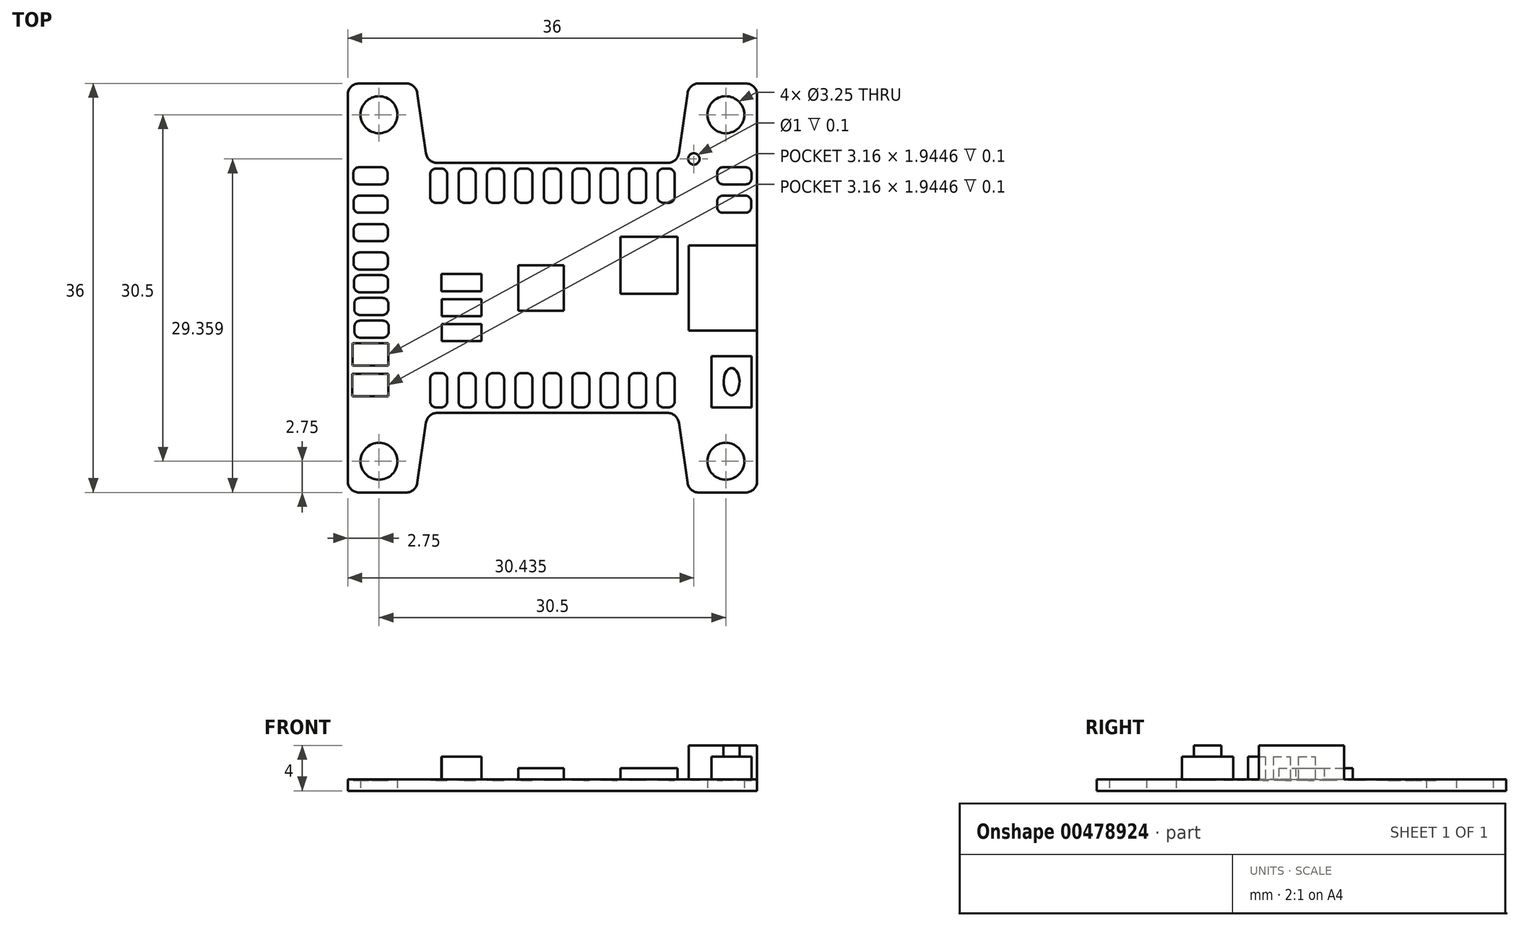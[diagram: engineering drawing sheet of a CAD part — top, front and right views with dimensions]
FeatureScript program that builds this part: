
annotation { "Feature Type Name" : "Feature", "Feature Type Description" : "" }
export const myFeature = defineFeature(function(context is Context, id is Id, definition is map)
    precondition{}
    {
        {
            var Q0;
            Q0=qCreatedBy(makeId("Top.planeOp"),FACE);
            var sketch = newSketch(context, id + "F0", { "sketchPlane" : qUnion([Q0])});
            skLineSegment(sketch, "E0.bottom", {"start": v(17, -18) * mm, "end": v(12.87, -18) * mm});
            skLineSegment(sketch, "E0.top", {"start": v(17, 18) * mm, "end": v(12.87, 18) * mm});
            skLineSegment(sketch, "E0.left", {"start": v(18, -17) * mm, "end": v(18, 17) * mm});
            skLineSegment(sketch, "E0.right", {"start": v(-18, -17) * mm, "end": v(-18, 17) * mm});
            skPoint(sketch, "E0.middle", {"position": v(0, 0) * mm});
            skLineSegment(sketch, "E1.bottom", {"start": v(15.25, 15.25) * mm, "end": v(-15.25, 15.25) * mm, "construction": true});
            skLineSegment(sketch, "E1.top", {"start": v(15.25, -15.25) * mm, "end": v(-15.25, -15.25) * mm, "construction": true});
            skLineSegment(sketch, "E1.left", {"start": v(15.25, 15.25) * mm, "end": v(15.25, -15.25) * mm, "construction": true});
            skLineSegment(sketch, "E1.right", {"start": v(-15.25, 15.25) * mm, "end": v(-15.25, -15.25) * mm, "construction": true});
            skCircle(sketch, "E2", {"center": v(-15.25, 15.25) * mm, "radius": 1.63 * mm});
            skCircle(sketch, "E3.MirrorC", {"center": v(15.25, 15.25) * mm, "radius": 1.63 * mm});
            skCircle(sketch, "E4.MirrorC", {"center": v(-15.25, -15.25) * mm, "radius": 1.63 * mm});
            skCircle(sketch, "E5.MirrorC", {"center": v(15.25, -15.25) * mm, "radius": 1.63 * mm});
            skLineSegment(sketch, "E6.left", {"start": v(18, -11) * mm, "end": v(18, 11) * mm});
            skLineSegment(sketch, "E6.right", {"start": v(-18, -11) * mm, "end": v(-18, 11) * mm});
            skLineSegment(sketch, "E7", {"start": v(-11.88, 17.14) * mm, "end": v(-11.12, 11.86) * mm});
            skLineSegment(sketch, "E8.MirrorCS", {"start": v(11.88, 17.14) * mm, "end": v(11.12, 11.86) * mm});
            skLineSegment(sketch, "E9.MirrorCS", {"start": v(-11.88, -17.14) * mm, "end": v(-11.12, -11.86) * mm});
            skLineSegment(sketch, "E10.MirrorCS", {"start": v(11.88, -17.14) * mm, "end": v(11.12, -11.86) * mm});
            skLineSegment(sketch, "E11.trimOffspring", {"start": v(10.13, 11) * mm, "end": v(-10.13, 11) * mm});
            skLineSegment(sketch, "E12.trimOffspring", {"start": v(10.13, -11) * mm, "end": v(-10.13, -11) * mm});
            skLineSegment(sketch, "E13.trimOffspring", {"start": v(-12.87, 18) * mm, "end": v(-17, 18) * mm});
            skLineSegment(sketch, "E14.trimOffspring", {"start": v(-12.87, -18) * mm, "end": v(-17, -18) * mm});
            skPoint(sketch, "E15.visualSharp", {"position": v(-18, 18) * mm});
            skArc(sketch, "E15.filletArc", {"start": v(-17, 18) * mm, "mid": v(-17.7, 17.7) * mm, "end": v(-18, 17) * mm});
            skPoint(sketch, "E16.visualSharp", {"position": v(-12, 18) * mm});
            skArc(sketch, "E16.filletArc", {"start": v(-11.88, 17.14) * mm, "mid": v(-12.21, 17.76) * mm, "end": v(-12.87, 18) * mm});
            skPoint(sketch, "E17.visualSharp", {"position": v(-11, 11) * mm});
            skArc(sketch, "E17.filletArc", {"start": v(-11.12, 11.86) * mm, "mid": v(-10.78, 11.24) * mm, "end": v(-10.13, 11) * mm});
            skPoint(sketch, "E18.visualSharp", {"position": v(12, 18) * mm});
            skArc(sketch, "E18.filletArc", {"start": v(12.87, 18) * mm, "mid": v(12.21, 17.76) * mm, "end": v(11.88, 17.14) * mm});
            skPoint(sketch, "E19.visualSharp", {"position": v(11, 11) * mm});
            skArc(sketch, "E19.filletArc", {"start": v(10.13, 11) * mm, "mid": v(10.78, 11.24) * mm, "end": v(11.12, 11.86) * mm});
            skPoint(sketch, "E20.visualSharp", {"position": v(18, 18) * mm});
            skArc(sketch, "E20.filletArc", {"start": v(18, 17) * mm, "mid": v(17.7, 17.7) * mm, "end": v(17, 18) * mm});
            skPoint(sketch, "E21.visualSharp", {"position": v(18, -18) * mm});
            skArc(sketch, "E21.filletArc", {"start": v(17, -18) * mm, "mid": v(17.7, -17.7) * mm, "end": v(18, -17) * mm});
            skPoint(sketch, "E22.visualSharp", {"position": v(12, -18) * mm});
            skArc(sketch, "E22.filletArc", {"start": v(11.88, -17.14) * mm, "mid": v(12.21, -17.76) * mm, "end": v(12.87, -18) * mm});
            skPoint(sketch, "E23.visualSharp", {"position": v(11, -11) * mm});
            skArc(sketch, "E23.filletArc", {"start": v(11.12, -11.86) * mm, "mid": v(10.78, -11.24) * mm, "end": v(10.13, -11) * mm});
            skPoint(sketch, "E24.visualSharp", {"position": v(-11, -11) * mm});
            skArc(sketch, "E24.filletArc", {"start": v(-10.13, -11) * mm, "mid": v(-10.78, -11.24) * mm, "end": v(-11.12, -11.86) * mm});
            skPoint(sketch, "E25.visualSharp", {"position": v(-12, -18) * mm});
            skArc(sketch, "E25.filletArc", {"start": v(-12.87, -18) * mm, "mid": v(-12.21, -17.76) * mm, "end": v(-11.88, -17.14) * mm});
            skPoint(sketch, "E26.visualSharp", {"position": v(-18, -18) * mm});
            skArc(sketch, "E26.filletArc", {"start": v(-18, -17) * mm, "mid": v(-17.7, -17.7) * mm, "end": v(-17, -18) * mm});
            skSolve(sketch);
        }
        {
            var Q0;
            Q0=makeQuery(id+"F0.imprint","IMPRINT",FACE,{"disambiguationData":[TD([[makeQuery(id+"F0.imprint","IMPRINT",EDGE,{"derivedFrom":sQuery(id+"F0.wireOp",EDGE,"E0.bottom")}),-1.0]])]});
            extrude(context, id + "F1", {"entities" : qUnion([Q0]), "depth" : 1 * mm, "offsetDistance" : 25 * mm});
        }
        {
            var Q0;
            Q0=makeQuery(id+"F1.opExtrude","CAP_FACE",FACE,{"disambiguationData":[OSD([sQuery(id+"F0.wireOp",EDGE,"E0.bottom"),sQuery(id+"F0.wireOp",EDGE,"E0.top"),sQuery(id+"F0.wireOp",EDGE,"E0.left"),sQuery(id+"F0.wireOp",EDGE,"E0.right"),sQuery(id+"F0.wireOp",EDGE,"E2"),sQuery(id+"F0.wireOp",EDGE,"E3.MirrorC"),sQuery(id+"F0.wireOp",EDGE,"E4.MirrorC"),sQuery(id+"F0.wireOp",EDGE,"E5.MirrorC"),sQuery(id+"F0.wireOp",EDGE,"E7"),sQuery(id+"F0.wireOp",EDGE,"E8.MirrorCS"),sQuery(id+"F0.wireOp",EDGE,"E9.MirrorCS"),sQuery(id+"F0.wireOp",EDGE,"E10.MirrorCS"),sQuery(id+"F0.wireOp",EDGE,"E11.trimOffspring"),sQuery(id+"F0.wireOp",EDGE,"E12.trimOffspring"),sQuery(id+"F0.wireOp",EDGE,"E13.trimOffspring"),sQuery(id+"F0.wireOp",EDGE,"E14.trimOffspring"),sQuery(id+"F0.wireOp",EDGE,"E15.filletArc"),sQuery(id+"F0.wireOp",EDGE,"E16.filletArc"),sQuery(id+"F0.wireOp",EDGE,"E17.filletArc"),sQuery(id+"F0.wireOp",EDGE,"E18.filletArc"),sQuery(id+"F0.wireOp",EDGE,"E19.filletArc"),sQuery(id+"F0.wireOp",EDGE,"E20.filletArc"),sQuery(id+"F0.wireOp",EDGE,"E21.filletArc"),sQuery(id+"F0.wireOp",EDGE,"E22.filletArc"),sQuery(id+"F0.wireOp",EDGE,"E23.filletArc"),sQuery(id+"F0.wireOp",EDGE,"E24.filletArc"),sQuery(id+"F0.wireOp",EDGE,"E25.filletArc"),sQuery(id+"F0.wireOp",EDGE,"E26.filletArc")])],"isStart":false});
            var sketch = newSketch(context, id + "F2", { "sketchPlane" : qUnion([Q0])});
            skLineSegment(sketch, "E27.bottom", {"start": v(0.25, 7.5) * mm, "end": v(-0.25, 7.5) * mm});
            skLineSegment(sketch, "E27.top", {"start": v(0.25, 10.5) * mm, "end": v(-0.25, 10.5) * mm});
            skLineSegment(sketch, "E27.left", {"start": v(0.75, 8) * mm, "end": v(0.75, 10) * mm});
            skLineSegment(sketch, "E27.right", {"start": v(-0.75, 8) * mm, "end": v(-0.75, 10) * mm});
            skPoint(sketch, "E27.middle", {"position": v(0, 9) * mm});
            skPoint(sketch, "E28.visualSharp", {"position": v(-0.75, 10.5) * mm});
            skArc(sketch, "E28.filletArc", {"start": v(-0.25, 10.5) * mm, "mid": v(-0.6, 10.35) * mm, "end": v(-0.75, 10) * mm});
            skPoint(sketch, "E29.visualSharp", {"position": v(0.75, 10.5) * mm});
            skArc(sketch, "E29.filletArc", {"start": v(0.75, 10) * mm, "mid": v(0.6, 10.35) * mm, "end": v(0.25, 10.5) * mm});
            skPoint(sketch, "E30.visualSharp", {"position": v(0.75, 7.5) * mm});
            skArc(sketch, "E30.filletArc", {"start": v(0.25, 7.5) * mm, "mid": v(0.6, 7.65) * mm, "end": v(0.75, 8) * mm});
            skPoint(sketch, "E31.visualSharp", {"position": v(-0.75, 7.5) * mm});
            skArc(sketch, "E31.filletArc", {"start": v(-0.75, 8) * mm, "mid": v(-0.6, 7.65) * mm, "end": v(-0.25, 7.5) * mm});
            skLineSegment(sketch, "E32.1.0.0", {"start": v(3.25, 8) * mm, "end": v(3.25, 10) * mm});
            skPoint(sketch, "E32.1.0.1", {"position": v(3.25, 7.5) * mm});
            skLineSegment(sketch, "E32.1.0.2", {"start": v(1.75, 8) * mm, "end": v(1.75, 10) * mm});
            skArc(sketch, "E32.1.0.3", {"start": v(2.75, 7.5) * mm, "mid": v(3.1, 7.65) * mm, "end": v(3.25, 8) * mm});
            skPoint(sketch, "E32.1.0.4", {"position": v(1.75, 10.5) * mm});
            skArc(sketch, "E32.1.0.5", {"start": v(2.25, 10.5) * mm, "mid": v(1.9, 10.35) * mm, "end": v(1.75, 10) * mm});
            skPoint(sketch, "E32.1.0.6", {"position": v(3.25, 10.5) * mm});
            skArc(sketch, "E32.1.0.7", {"start": v(1.75, 8) * mm, "mid": v(1.9, 7.65) * mm, "end": v(2.25, 7.5) * mm});
            skLineSegment(sketch, "E32.1.0.8", {"start": v(2.75, 10.5) * mm, "end": v(2.25, 10.5) * mm});
            skLineSegment(sketch, "E32.1.0.9", {"start": v(2.75, 7.5) * mm, "end": v(2.25, 7.5) * mm});
            skPoint(sketch, "E32.1.0.10", {"position": v(2.5, 9) * mm});
            skPoint(sketch, "E32.1.0.11", {"position": v(1.75, 7.5) * mm});
            skArc(sketch, "E32.1.0.12", {"start": v(3.25, 10) * mm, "mid": v(3.1, 10.35) * mm, "end": v(2.75, 10.5) * mm});
            skLineSegment(sketch, "E32.2.0.0", {"start": v(5.75, 8) * mm, "end": v(5.75, 10) * mm});
            skPoint(sketch, "E32.2.0.1", {"position": v(5.75, 7.5) * mm});
            skLineSegment(sketch, "E32.2.0.2", {"start": v(4.25, 8) * mm, "end": v(4.25, 10) * mm});
            skArc(sketch, "E32.2.0.3", {"start": v(5.25, 7.5) * mm, "mid": v(5.6, 7.65) * mm, "end": v(5.75, 8) * mm});
            skPoint(sketch, "E32.2.0.4", {"position": v(4.25, 10.5) * mm});
            skArc(sketch, "E32.2.0.5", {"start": v(4.75, 10.5) * mm, "mid": v(4.4, 10.35) * mm, "end": v(4.25, 10) * mm});
            skPoint(sketch, "E32.2.0.6", {"position": v(5.75, 10.5) * mm});
            skArc(sketch, "E32.2.0.7", {"start": v(4.25, 8) * mm, "mid": v(4.4, 7.65) * mm, "end": v(4.75, 7.5) * mm});
            skLineSegment(sketch, "E32.2.0.8", {"start": v(5.25, 10.5) * mm, "end": v(4.75, 10.5) * mm});
            skLineSegment(sketch, "E32.2.0.9", {"start": v(5.25, 7.5) * mm, "end": v(4.75, 7.5) * mm});
            skPoint(sketch, "E32.2.0.10", {"position": v(5, 9) * mm});
            skPoint(sketch, "E32.2.0.11", {"position": v(4.25, 7.5) * mm});
            skArc(sketch, "E32.2.0.12", {"start": v(5.75, 10) * mm, "mid": v(5.6, 10.35) * mm, "end": v(5.25, 10.5) * mm});
            skLineSegment(sketch, "E32.3.0.0", {"start": v(8.25, 8) * mm, "end": v(8.25, 10) * mm});
            skPoint(sketch, "E32.3.0.1", {"position": v(8.25, 7.5) * mm});
            skLineSegment(sketch, "E32.3.0.2", {"start": v(6.75, 8) * mm, "end": v(6.75, 10) * mm});
            skArc(sketch, "E32.3.0.3", {"start": v(7.75, 7.5) * mm, "mid": v(8.1, 7.65) * mm, "end": v(8.25, 8) * mm});
            skPoint(sketch, "E32.3.0.4", {"position": v(6.75, 10.5) * mm});
            skArc(sketch, "E32.3.0.5", {"start": v(7.25, 10.5) * mm, "mid": v(6.9, 10.35) * mm, "end": v(6.75, 10) * mm});
            skPoint(sketch, "E32.3.0.6", {"position": v(8.25, 10.5) * mm});
            skArc(sketch, "E32.3.0.7", {"start": v(6.75, 8) * mm, "mid": v(6.9, 7.65) * mm, "end": v(7.25, 7.5) * mm});
            skLineSegment(sketch, "E32.3.0.8", {"start": v(7.75, 10.5) * mm, "end": v(7.25, 10.5) * mm});
            skLineSegment(sketch, "E32.3.0.9", {"start": v(7.75, 7.5) * mm, "end": v(7.25, 7.5) * mm});
            skPoint(sketch, "E32.3.0.10", {"position": v(7.5, 9) * mm});
            skPoint(sketch, "E32.3.0.11", {"position": v(6.75, 7.5) * mm});
            skArc(sketch, "E32.3.0.12", {"start": v(8.25, 10) * mm, "mid": v(8.1, 10.35) * mm, "end": v(7.75, 10.5) * mm});
            skLineSegment(sketch, "E32.4.0.0", {"start": v(10.75, 8) * mm, "end": v(10.75, 10) * mm});
            skPoint(sketch, "E32.4.0.1", {"position": v(10.75, 7.5) * mm});
            skLineSegment(sketch, "E32.4.0.2", {"start": v(9.25, 8) * mm, "end": v(9.25, 10) * mm});
            skArc(sketch, "E32.4.0.3", {"start": v(10.25, 7.5) * mm, "mid": v(10.6, 7.65) * mm, "end": v(10.75, 8) * mm});
            skPoint(sketch, "E32.4.0.4", {"position": v(9.25, 10.5) * mm});
            skArc(sketch, "E32.4.0.5", {"start": v(9.75, 10.5) * mm, "mid": v(9.4, 10.35) * mm, "end": v(9.25, 10) * mm});
            skPoint(sketch, "E32.4.0.6", {"position": v(10.75, 10.5) * mm});
            skArc(sketch, "E32.4.0.7", {"start": v(9.25, 8) * mm, "mid": v(9.4, 7.65) * mm, "end": v(9.75, 7.5) * mm});
            skLineSegment(sketch, "E32.4.0.8", {"start": v(10.25, 10.5) * mm, "end": v(9.75, 10.5) * mm});
            skLineSegment(sketch, "E32.4.0.9", {"start": v(10.25, 7.5) * mm, "end": v(9.75, 7.5) * mm});
            skPoint(sketch, "E32.4.0.10", {"position": v(10, 9) * mm});
            skPoint(sketch, "E32.4.0.11", {"position": v(9.25, 7.5) * mm});
            skArc(sketch, "E32.4.0.12", {"start": v(10.75, 10) * mm, "mid": v(10.6, 10.35) * mm, "end": v(10.25, 10.5) * mm});
            skLineSegment(sketch, "E32.direction1", {"start": v(-0.75, 7.5) * mm, "end": v(1.75, 7.5) * mm, "construction": true});
            skArc(sketch, "E33.MirrorCS", {"start": v(-9.25, 8) * mm, "mid": v(-9.4, 7.65) * mm, "end": v(-9.75, 7.5) * mm});
            skLineSegment(sketch, "E34.MirrorCS", {"start": v(-7.75, 10.5) * mm, "end": v(-7.25, 10.5) * mm});
            skArc(sketch, "E35.MirrorCS", {"start": v(-4.25, 8) * mm, "mid": v(-4.4, 7.65) * mm, "end": v(-4.75, 7.5) * mm});
            skArc(sketch, "E36.MirrorCS", {"start": v(-7.25, 10.5) * mm, "mid": v(-6.9, 10.35) * mm, "end": v(-6.75, 10) * mm});
            skArc(sketch, "E37.MirrorCS", {"start": v(-9.75, 10.5) * mm, "mid": v(-9.4, 10.35) * mm, "end": v(-9.25, 10) * mm});
            skArc(sketch, "E38.MirrorCS", {"start": v(-4.75, 10.5) * mm, "mid": v(-4.4, 10.35) * mm, "end": v(-4.25, 10) * mm});
            skArc(sketch, "E39.MirrorCS", {"start": v(-7.75, 7.5) * mm, "mid": v(-8.1, 7.65) * mm, "end": v(-8.25, 8) * mm});
            skArc(sketch, "E40.MirrorCS", {"start": v(-1.75, 8) * mm, "mid": v(-1.9, 7.65) * mm, "end": v(-2.25, 7.5) * mm});
            skArc(sketch, "E41.MirrorCS", {"start": v(-2.25, 10.5) * mm, "mid": v(-1.9, 10.35) * mm, "end": v(-1.75, 10) * mm});
            skArc(sketch, "E42.MirrorCS", {"start": v(-2.75, 7.5) * mm, "mid": v(-3.1, 7.65) * mm, "end": v(-3.25, 8) * mm});
            skArc(sketch, "E43.MirrorCS", {"start": v(-10.25, 7.5) * mm, "mid": v(-10.6, 7.65) * mm, "end": v(-10.75, 8) * mm});
            skArc(sketch, "E44.MirrorCS", {"start": v(-3.25, 10) * mm, "mid": v(-3.1, 10.35) * mm, "end": v(-2.75, 10.5) * mm});
            skLineSegment(sketch, "E45.MirrorCS", {"start": v(-2.75, 7.5) * mm, "end": v(-2.25, 7.5) * mm});
            skArc(sketch, "E46.MirrorCS", {"start": v(-5.25, 7.5) * mm, "mid": v(-5.6, 7.65) * mm, "end": v(-5.75, 8) * mm});
            skLineSegment(sketch, "E47.MirrorCS", {"start": v(-2.75, 10.5) * mm, "end": v(-2.25, 10.5) * mm});
            skArc(sketch, "E48.MirrorCS", {"start": v(-5.75, 10) * mm, "mid": v(-5.6, 10.35) * mm, "end": v(-5.25, 10.5) * mm});
            skArc(sketch, "E49.MirrorCS", {"start": v(-10.75, 10) * mm, "mid": v(-10.6, 10.35) * mm, "end": v(-10.25, 10.5) * mm});
            skLineSegment(sketch, "E50.MirrorCS", {"start": v(-10.25, 7.5) * mm, "end": v(-9.75, 7.5) * mm});
            skArc(sketch, "E51.MirrorCS", {"start": v(-8.25, 10) * mm, "mid": v(-8.1, 10.35) * mm, "end": v(-7.75, 10.5) * mm});
            skLineSegment(sketch, "E52.MirrorCS", {"start": v(-5.25, 10.5) * mm, "end": v(-4.75, 10.5) * mm});
            skArc(sketch, "E53.MirrorCS", {"start": v(-6.75, 8) * mm, "mid": v(-6.9, 7.65) * mm, "end": v(-7.25, 7.5) * mm});
            skLineSegment(sketch, "E54.MirrorCS", {"start": v(-7.75, 7.5) * mm, "end": v(-7.25, 7.5) * mm});
            skLineSegment(sketch, "E55.MirrorCS", {"start": v(-5.25, 7.5) * mm, "end": v(-4.75, 7.5) * mm});
            skLineSegment(sketch, "E56.MirrorCS", {"start": v(-10.25, 10.5) * mm, "end": v(-9.75, 10.5) * mm});
            skLineSegment(sketch, "E57.MirrorCS", {"start": v(0.75, 7.5) * mm, "end": v(-1.75, 7.5) * mm, "construction": true});
            skPoint(sketch, "E58.MirrorP", {"position": v(-3.25, 7.5) * mm});
            skPoint(sketch, "E59.MirrorP", {"position": v(-4.25, 7.5) * mm});
            skPoint(sketch, "E60.MirrorP", {"position": v(-5.75, 7.5) * mm});
            skPoint(sketch, "E61.MirrorP", {"position": v(-1.75, 10.5) * mm});
            skPoint(sketch, "E62.MirrorP", {"position": v(-6.75, 7.5) * mm});
            skPoint(sketch, "E63.MirrorP", {"position": v(-8.25, 7.5) * mm});
            skPoint(sketch, "E64.MirrorP", {"position": v(-9.25, 7.5) * mm});
            skPoint(sketch, "E65.MirrorP", {"position": v(-10.75, 10.5) * mm});
            skPoint(sketch, "E66.MirrorP", {"position": v(-5, 9) * mm});
            skLineSegment(sketch, "E67.MirrorCS", {"start": v(-1.75, 8) * mm, "end": v(-1.75, 10) * mm});
            skLineSegment(sketch, "E68.MirrorCS", {"start": v(-3.25, 8) * mm, "end": v(-3.25, 10) * mm});
            skPoint(sketch, "E69.MirrorP", {"position": v(-7.5, 9) * mm});
            skLineSegment(sketch, "E70.MirrorCS", {"start": v(-6.75, 8) * mm, "end": v(-6.75, 10) * mm});
            skPoint(sketch, "E71.MirrorP", {"position": v(-1.75, 7.5) * mm});
            skLineSegment(sketch, "E72.MirrorCS", {"start": v(-9.25, 8) * mm, "end": v(-9.25, 10) * mm});
            skPoint(sketch, "E73.MirrorP", {"position": v(-5.75, 10.5) * mm});
            skLineSegment(sketch, "E74.MirrorCS", {"start": v(-4.25, 8) * mm, "end": v(-4.25, 10) * mm});
            skPoint(sketch, "E75.MirrorP", {"position": v(-2.5, 9) * mm});
            skPoint(sketch, "E76.MirrorP", {"position": v(-8.25, 10.5) * mm});
            skLineSegment(sketch, "E77.MirrorCS", {"start": v(-8.25, 8) * mm, "end": v(-8.25, 10) * mm});
            skPoint(sketch, "E78.MirrorP", {"position": v(-9.25, 10.5) * mm});
            skLineSegment(sketch, "E79.MirrorCS", {"start": v(-5.75, 8) * mm, "end": v(-5.75, 10) * mm});
            skLineSegment(sketch, "E80.MirrorCS", {"start": v(-10.75, 8) * mm, "end": v(-10.75, 10) * mm});
            skPoint(sketch, "E81.MirrorP", {"position": v(-10, 9) * mm});
            skPoint(sketch, "E82.MirrorP", {"position": v(-6.75, 10.5) * mm});
            skPoint(sketch, "E83.MirrorP", {"position": v(-4.25, 10.5) * mm});
            skPoint(sketch, "E84.MirrorP", {"position": v(-3.25, 10.5) * mm});
            skPoint(sketch, "E85.MirrorP", {"position": v(-10.75, 7.5) * mm});
            skArc(sketch, "E86.MirrorCS", {"start": v(9.25, -8) * mm, "mid": v(9.4, -7.65) * mm, "end": v(9.75, -7.5) * mm});
            skLineSegment(sketch, "E87.MirrorCS", {"start": v(7.75, -10.5) * mm, "end": v(7.25, -10.5) * mm});
            skArc(sketch, "E88.MirrorCS", {"start": v(-3.25, -10) * mm, "mid": v(-3.1, -10.35) * mm, "end": v(-2.75, -10.5) * mm});
            skArc(sketch, "E89.MirrorCS", {"start": v(-9.75, -10.5) * mm, "mid": v(-9.4, -10.35) * mm, "end": v(-9.25, -10) * mm});
            skArc(sketch, "E90.MirrorCS", {"start": v(4.25, -8) * mm, "mid": v(4.4, -7.65) * mm, "end": v(4.75, -7.5) * mm});
            skArc(sketch, "E91.MirrorCS", {"start": v(7.25, -10.5) * mm, "mid": v(6.9, -10.35) * mm, "end": v(6.75, -10) * mm});
            skArc(sketch, "E92.MirrorCS", {"start": v(-4.25, -8) * mm, "mid": v(-4.4, -7.65) * mm, "end": v(-4.75, -7.5) * mm});
            skArc(sketch, "E93.MirrorCS", {"start": v(-8.25, -10) * mm, "mid": v(-8.1, -10.35) * mm, "end": v(-7.75, -10.5) * mm});
            skArc(sketch, "E94.MirrorCS", {"start": v(9.75, -10.5) * mm, "mid": v(9.4, -10.35) * mm, "end": v(9.25, -10) * mm});
            skArc(sketch, "E95.MirrorCS", {"start": v(-10.25, -7.5) * mm, "mid": v(-10.6, -7.65) * mm, "end": v(-10.75, -8) * mm});
            skArc(sketch, "E96.MirrorCS", {"start": v(4.75, -10.5) * mm, "mid": v(4.4, -10.35) * mm, "end": v(4.25, -10) * mm});
            skArc(sketch, "E97.MirrorCS", {"start": v(7.75, -7.5) * mm, "mid": v(8.1, -7.65) * mm, "end": v(8.25, -8) * mm});
            skLineSegment(sketch, "E98.MirrorCS", {"start": v(-7.75, -10.5) * mm, "end": v(-7.25, -10.5) * mm});
            skLineSegment(sketch, "E99.MirrorCS", {"start": v(-10.25, -7.5) * mm, "end": v(-9.75, -7.5) * mm});
            skArc(sketch, "E100.MirrorCS", {"start": v(1.75, -8) * mm, "mid": v(1.9, -7.65) * mm, "end": v(2.25, -7.5) * mm});
            skArc(sketch, "E101.MirrorCS", {"start": v(2.25, -10.5) * mm, "mid": v(1.9, -10.35) * mm, "end": v(1.75, -10) * mm});
            skArc(sketch, "E102.MirrorCS", {"start": v(2.75, -7.5) * mm, "mid": v(3.1, -7.65) * mm, "end": v(3.25, -8) * mm});
            skArc(sketch, "E103.MirrorCS", {"start": v(-0.75, -8) * mm, "mid": v(-0.6, -7.65) * mm, "end": v(-0.25, -7.5) * mm});
            skArc(sketch, "E104.MirrorCS", {"start": v(0.25, -7.5) * mm, "mid": v(0.6, -7.65) * mm, "end": v(0.75, -8) * mm});
            skArc(sketch, "E105.MirrorCS", {"start": v(0.75, -10) * mm, "mid": v(0.6, -10.35) * mm, "end": v(0.25, -10.5) * mm});
            skArc(sketch, "E106.MirrorCS", {"start": v(-0.25, -10.5) * mm, "mid": v(-0.6, -10.35) * mm, "end": v(-0.75, -10) * mm});
            skLineSegment(sketch, "E107.MirrorCS", {"start": v(0.25, -10.5) * mm, "end": v(-0.25, -10.5) * mm});
            skLineSegment(sketch, "E108.MirrorCS", {"start": v(0.25, -7.5) * mm, "end": v(-0.25, -7.5) * mm});
            skArc(sketch, "E109.MirrorCS", {"start": v(10.25, -7.5) * mm, "mid": v(10.6, -7.65) * mm, "end": v(10.75, -8) * mm});
            skArc(sketch, "E110.MirrorCS", {"start": v(-2.75, -7.5) * mm, "mid": v(-3.1, -7.65) * mm, "end": v(-3.25, -8) * mm});
            skArc(sketch, "E111.MirrorCS", {"start": v(3.25, -10) * mm, "mid": v(3.1, -10.35) * mm, "end": v(2.75, -10.5) * mm});
            skArc(sketch, "E112.MirrorCS", {"start": v(5.25, -7.5) * mm, "mid": v(5.6, -7.65) * mm, "end": v(5.75, -8) * mm});
            skLineSegment(sketch, "E113.MirrorCS", {"start": v(-5.25, -10.5) * mm, "end": v(-4.75, -10.5) * mm});
            skArc(sketch, "E114.MirrorCS", {"start": v(-7.25, -10.5) * mm, "mid": v(-6.9, -10.35) * mm, "end": v(-6.75, -10) * mm});
            skArc(sketch, "E115.MirrorCS", {"start": v(6.75, -8) * mm, "mid": v(6.9, -7.65) * mm, "end": v(7.25, -7.5) * mm});
            skLineSegment(sketch, "E116.MirrorCS", {"start": v(5.25, -10.5) * mm, "end": v(4.75, -10.5) * mm});
            skLineSegment(sketch, "E117.MirrorCS", {"start": v(-7.75, -7.5) * mm, "end": v(-7.25, -7.5) * mm});
            skLineSegment(sketch, "E118.MirrorCS", {"start": v(-2.75, -7.5) * mm, "end": v(-2.25, -7.5) * mm});
            skArc(sketch, "E119.MirrorCS", {"start": v(-4.75, -10.5) * mm, "mid": v(-4.4, -10.35) * mm, "end": v(-4.25, -10) * mm});
            skLineSegment(sketch, "E120.MirrorCS", {"start": v(10.25, -10.5) * mm, "end": v(9.75, -10.5) * mm});
            skLineSegment(sketch, "E121.MirrorCS", {"start": v(7.75, -7.5) * mm, "end": v(7.25, -7.5) * mm});
            skLineSegment(sketch, "E122.MirrorCS", {"start": v(5.25, -7.5) * mm, "end": v(4.75, -7.5) * mm});
            skLineSegment(sketch, "E123.MirrorCS", {"start": v(-5.25, -7.5) * mm, "end": v(-4.75, -7.5) * mm});
            skArc(sketch, "E124.MirrorCS", {"start": v(-7.75, -7.5) * mm, "mid": v(-8.1, -7.65) * mm, "end": v(-8.25, -8) * mm});
            skArc(sketch, "E125.MirrorCS", {"start": v(-5.25, -7.5) * mm, "mid": v(-5.6, -7.65) * mm, "end": v(-5.75, -8) * mm});
            skLineSegment(sketch, "E126.MirrorCS", {"start": v(10.25, -7.5) * mm, "end": v(9.75, -7.5) * mm});
            skArc(sketch, "E127.MirrorCS", {"start": v(8.25, -10) * mm, "mid": v(8.1, -10.35) * mm, "end": v(7.75, -10.5) * mm});
            skLineSegment(sketch, "E128.MirrorCS", {"start": v(-10.25, -10.5) * mm, "end": v(-9.75, -10.5) * mm});
            skArc(sketch, "E129.MirrorCS", {"start": v(-1.75, -8) * mm, "mid": v(-1.9, -7.65) * mm, "end": v(-2.25, -7.5) * mm});
            skLineSegment(sketch, "E130.MirrorCS", {"start": v(-2.75, -10.5) * mm, "end": v(-2.25, -10.5) * mm});
            skArc(sketch, "E131.MirrorCS", {"start": v(10.75, -10) * mm, "mid": v(10.6, -10.35) * mm, "end": v(10.25, -10.5) * mm});
            skArc(sketch, "E132.MirrorCS", {"start": v(5.75, -10) * mm, "mid": v(5.6, -10.35) * mm, "end": v(5.25, -10.5) * mm});
            skArc(sketch, "E133.MirrorCS", {"start": v(-5.75, -10) * mm, "mid": v(-5.6, -10.35) * mm, "end": v(-5.25, -10.5) * mm});
            skLineSegment(sketch, "E134.MirrorCS", {"start": v(2.75, -10.5) * mm, "end": v(2.25, -10.5) * mm});
            skLineSegment(sketch, "E135.MirrorCS", {"start": v(2.75, -7.5) * mm, "end": v(2.25, -7.5) * mm});
            skArc(sketch, "E136.MirrorCS", {"start": v(-2.25, -10.5) * mm, "mid": v(-1.9, -10.35) * mm, "end": v(-1.75, -10) * mm});
            skArc(sketch, "E137.MirrorCS", {"start": v(-9.25, -8) * mm, "mid": v(-9.4, -7.65) * mm, "end": v(-9.75, -7.5) * mm});
            skArc(sketch, "E138.MirrorCS", {"start": v(-10.75, -10) * mm, "mid": v(-10.6, -10.35) * mm, "end": v(-10.25, -10.5) * mm});
            skArc(sketch, "E139.MirrorCS", {"start": v(-6.75, -8) * mm, "mid": v(-6.9, -7.65) * mm, "end": v(-7.25, -7.5) * mm});
            skLineSegment(sketch, "E140.MirrorCS", {"start": v(-0.75, -7.5) * mm, "end": v(1.75, -7.5) * mm, "construction": true});
            skLineSegment(sketch, "E141.MirrorCS", {"start": v(0.75, -7.5) * mm, "end": v(-1.75, -7.5) * mm, "construction": true});
            skPoint(sketch, "E142.MirrorP", {"position": v(-1.75, -7.5) * mm});
            skPoint(sketch, "E143.MirrorP", {"position": v(-0.75, -7.5) * mm});
            skLineSegment(sketch, "E144.MirrorCS", {"start": v(-6.75, -8) * mm, "end": v(-6.75, -10) * mm});
            skPoint(sketch, "E145.MirrorP", {"position": v(-1.75, -10.5) * mm});
            skPoint(sketch, "E146.MirrorP", {"position": v(-2.5, -9) * mm});
            skPoint(sketch, "E147.MirrorP", {"position": v(-10.75, -7.5) * mm});
            skPoint(sketch, "E148.MirrorP", {"position": v(0, -9) * mm});
            skPoint(sketch, "E149.MirrorP", {"position": v(1.75, -7.5) * mm});
            skPoint(sketch, "E150.MirrorP", {"position": v(3.25, -7.5) * mm});
            skPoint(sketch, "E151.MirrorP", {"position": v(4.25, -7.5) * mm});
            skPoint(sketch, "E152.MirrorP", {"position": v(9.25, -10.5) * mm});
            skPoint(sketch, "E153.MirrorP", {"position": v(-7.5, -9) * mm});
            skPoint(sketch, "E154.MirrorP", {"position": v(5.75, -10.5) * mm});
            skLineSegment(sketch, "E155.MirrorCS", {"start": v(-3.25, -8) * mm, "end": v(-3.25, -10) * mm});
            skPoint(sketch, "E156.MirrorP", {"position": v(-5.75, -7.5) * mm});
            skPoint(sketch, "E157.MirrorP", {"position": v(-3.25, -10.5) * mm});
            skLineSegment(sketch, "E158.MirrorCS", {"start": v(1.75, -8) * mm, "end": v(1.75, -10) * mm});
            skLineSegment(sketch, "E159.MirrorCS", {"start": v(3.25, -8) * mm, "end": v(3.25, -10) * mm});
            skPoint(sketch, "E160.MirrorP", {"position": v(2.5, -9) * mm});
            skPoint(sketch, "E161.MirrorP", {"position": v(8.25, -10.5) * mm});
            skLineSegment(sketch, "E162.MirrorCS", {"start": v(-0.75, -8) * mm, "end": v(-0.75, -10) * mm});
            skLineSegment(sketch, "E163.MirrorCS", {"start": v(0.75, -8) * mm, "end": v(0.75, -10) * mm});
            skPoint(sketch, "E164.MirrorP", {"position": v(0.75, -7.5) * mm});
            skLineSegment(sketch, "E165.MirrorCS", {"start": v(-1.75, -8) * mm, "end": v(-1.75, -10) * mm});
            skPoint(sketch, "E166.MirrorP", {"position": v(10, -9) * mm});
            skPoint(sketch, "E167.MirrorP", {"position": v(7.5, -9) * mm});
            skPoint(sketch, "E168.MirrorP", {"position": v(-0.75, -10.5) * mm});
            skPoint(sketch, "E169.MirrorP", {"position": v(-6.75, -7.5) * mm});
            skPoint(sketch, "E170.MirrorP", {"position": v(-8.25, -10.5) * mm});
            skLineSegment(sketch, "E171.MirrorCS", {"start": v(-9.25, -8) * mm, "end": v(-9.25, -10) * mm});
            skPoint(sketch, "E172.MirrorP", {"position": v(5, -9) * mm});
            skPoint(sketch, "E173.MirrorP", {"position": v(-5.75, -10.5) * mm});
            skPoint(sketch, "E174.MirrorP", {"position": v(10.75, -10.5) * mm});
            skPoint(sketch, "E175.MirrorP", {"position": v(9.25, -7.5) * mm});
            skPoint(sketch, "E176.MirrorP", {"position": v(6.75, -7.5) * mm});
            skPoint(sketch, "E177.MirrorP", {"position": v(8.25, -7.5) * mm});
            skPoint(sketch, "E178.MirrorP", {"position": v(5.75, -7.5) * mm});
            skPoint(sketch, "E179.MirrorP", {"position": v(1.75, -10.5) * mm});
            skPoint(sketch, "E180.MirrorP", {"position": v(-9.25, -10.5) * mm});
            skPoint(sketch, "E181.MirrorP", {"position": v(-8.25, -7.5) * mm});
            skLineSegment(sketch, "E182.MirrorCS", {"start": v(-4.25, -8) * mm, "end": v(-4.25, -10) * mm});
            skLineSegment(sketch, "E183.MirrorCS", {"start": v(10.75, -8) * mm, "end": v(10.75, -10) * mm});
            skPoint(sketch, "E184.MirrorP", {"position": v(0.75, -10.5) * mm});
            skPoint(sketch, "E185.MirrorP", {"position": v(-9.25, -7.5) * mm});
            skPoint(sketch, "E186.MirrorP", {"position": v(-10, -9) * mm});
            skLineSegment(sketch, "E187.MirrorCS", {"start": v(5.75, -8) * mm, "end": v(5.75, -10) * mm});
            skLineSegment(sketch, "E188.MirrorCS", {"start": v(-8.25, -8) * mm, "end": v(-8.25, -10) * mm});
            skPoint(sketch, "E189.MirrorP", {"position": v(4.25, -10.5) * mm});
            skPoint(sketch, "E190.MirrorP", {"position": v(-10.75, -10.5) * mm});
            skPoint(sketch, "E191.MirrorP", {"position": v(10.75, -7.5) * mm});
            skLineSegment(sketch, "E192.MirrorCS", {"start": v(8.25, -8) * mm, "end": v(8.25, -10) * mm});
            skLineSegment(sketch, "E193.MirrorCS", {"start": v(-5.75, -8) * mm, "end": v(-5.75, -10) * mm});
            skPoint(sketch, "E194.MirrorP", {"position": v(-6.75, -10.5) * mm});
            skPoint(sketch, "E195.MirrorP", {"position": v(-4.25, -10.5) * mm});
            skPoint(sketch, "E196.MirrorP", {"position": v(-3.25, -7.5) * mm});
            skPoint(sketch, "E197.MirrorP", {"position": v(6.75, -10.5) * mm});
            skLineSegment(sketch, "E198.MirrorCS", {"start": v(9.25, -8) * mm, "end": v(9.25, -10) * mm});
            skPoint(sketch, "E199.MirrorP", {"position": v(-4.25, -7.5) * mm});
            skLineSegment(sketch, "E200.MirrorCS", {"start": v(6.75, -8) * mm, "end": v(6.75, -10) * mm});
            skLineSegment(sketch, "E201.MirrorCS", {"start": v(-10.75, -8) * mm, "end": v(-10.75, -10) * mm});
            skLineSegment(sketch, "E202.MirrorCS", {"start": v(4.25, -8) * mm, "end": v(4.25, -10) * mm});
            skPoint(sketch, "E203.MirrorP", {"position": v(-5, -9) * mm});
            skPoint(sketch, "E204.MirrorP", {"position": v(3.25, -10.5) * mm});
            skLineSegment(sketch, "E205.MirrorCS", {"start": v(-14.5, 10.12) * mm, "end": v(-14.5, 9.62) * mm});
            skArc(sketch, "E206.MirrorCS", {"start": v(-14.5, 9.62) * mm, "mid": v(-14.65, 9.27) * mm, "end": v(-15, 9.12) * mm});
            skArc(sketch, "E207.MirrorCS", {"start": v(-17.5, 10.12) * mm, "mid": v(-17.35, 10.48) * mm, "end": v(-17, 10.62) * mm});
            skArc(sketch, "E208.MirrorCS", {"start": v(-15, 10.62) * mm, "mid": v(-14.65, 10.48) * mm, "end": v(-14.5, 10.12) * mm});
            skArc(sketch, "E209.MirrorCS", {"start": v(-17, 9.12) * mm, "mid": v(-17.35, 9.27) * mm, "end": v(-17.5, 9.62) * mm});
            skLineSegment(sketch, "E210.MirrorCS", {"start": v(-17.5, 10.12) * mm, "end": v(-17.5, 9.62) * mm});
            skLineSegment(sketch, "E211.MirrorCS", {"start": v(-17, 9.13) * mm, "end": v(-15, 9.12) * mm});
            skLineSegment(sketch, "E212.MirrorCS", {"start": v(-17, 10.63) * mm, "end": v(-15, 10.62) * mm});
            skLineSegment(sketch, "E213.1.0.0", {"start": v(-16.99, 8.13) * mm, "end": v(-14.99, 8.13) * mm});
            skLineSegment(sketch, "E213.1.0.1", {"start": v(-16.99, 6.63) * mm, "end": v(-14.99, 6.63) * mm});
            skArc(sketch, "E213.1.0.2", {"start": v(-16.99, 6.63) * mm, "mid": v(-17.34, 6.77) * mm, "end": v(-17.49, 7.13) * mm});
            skArc(sketch, "E213.1.0.3", {"start": v(-17.49, 7.63) * mm, "mid": v(-17.34, 7.98) * mm, "end": v(-16.99, 8.13) * mm});
            skArc(sketch, "E213.1.0.4", {"start": v(-14.49, 7.13) * mm, "mid": v(-14.63, 6.77) * mm, "end": v(-14.99, 6.63) * mm});
            skArc(sketch, "E213.1.0.5", {"start": v(-14.99, 8.13) * mm, "mid": v(-14.63, 7.98) * mm, "end": v(-14.49, 7.63) * mm});
            skLineSegment(sketch, "E213.1.0.6", {"start": v(-17.49, 7.63) * mm, "end": v(-17.49, 7.13) * mm});
            skLineSegment(sketch, "E213.1.0.7", {"start": v(-14.49, 7.63) * mm, "end": v(-14.49, 7.13) * mm});
            skLineSegment(sketch, "E213.2.0.0", {"start": v(-16.97, 5.63) * mm, "end": v(-14.97, 5.63) * mm});
            skLineSegment(sketch, "E213.2.0.1", {"start": v(-16.97, 4.13) * mm, "end": v(-14.97, 4.13) * mm});
            skArc(sketch, "E213.2.0.2", {"start": v(-16.97, 4.13) * mm, "mid": v(-17.32, 4.27) * mm, "end": v(-17.47, 4.63) * mm});
            skArc(sketch, "E213.2.0.3", {"start": v(-17.47, 5.13) * mm, "mid": v(-17.32, 5.48) * mm, "end": v(-16.97, 5.63) * mm});
            skArc(sketch, "E213.2.0.4", {"start": v(-14.47, 4.63) * mm, "mid": v(-14.62, 4.27) * mm, "end": v(-14.97, 4.13) * mm});
            skArc(sketch, "E213.2.0.5", {"start": v(-14.97, 5.63) * mm, "mid": v(-14.62, 5.48) * mm, "end": v(-14.47, 5.13) * mm});
            skLineSegment(sketch, "E213.2.0.6", {"start": v(-17.47, 5.13) * mm, "end": v(-17.47, 4.63) * mm});
            skLineSegment(sketch, "E213.2.0.7", {"start": v(-14.47, 5.13) * mm, "end": v(-14.47, 4.63) * mm});
            skLineSegment(sketch, "E213.direction1", {"start": v(-17, 9.12) * mm, "end": v(-16.99, 6.63) * mm, "construction": true});
            skLineSegment(sketch, "E214.MirrorCS", {"start": v(14.5, 10.12) * mm, "end": v(14.5, 9.62) * mm});
            skLineSegment(sketch, "E215.MirrorCS", {"start": v(14.49, 7.63) * mm, "end": v(14.49, 7.13) * mm});
            skLineSegment(sketch, "E216.MirrorCS", {"start": v(17.49, 7.63) * mm, "end": v(17.49, 7.13) * mm});
            skLineSegment(sketch, "E217.MirrorCS", {"start": v(17.5, 10.12) * mm, "end": v(17.5, 9.62) * mm});
            skArc(sketch, "E218.MirrorCS", {"start": v(15, 10.62) * mm, "mid": v(14.65, 10.48) * mm, "end": v(14.5, 10.12) * mm});
            skArc(sketch, "E219.MirrorCS", {"start": v(14.99, 8.13) * mm, "mid": v(14.63, 7.98) * mm, "end": v(14.49, 7.63) * mm});
            skArc(sketch, "E220.MirrorCS", {"start": v(14.49, 7.13) * mm, "mid": v(14.63, 6.77) * mm, "end": v(14.99, 6.63) * mm});
            skArc(sketch, "E221.MirrorCS", {"start": v(17.49, 7.63) * mm, "mid": v(17.34, 7.98) * mm, "end": v(16.99, 8.13) * mm});
            skArc(sketch, "E222.MirrorCS", {"start": v(16.99, 6.63) * mm, "mid": v(17.34, 6.77) * mm, "end": v(17.49, 7.13) * mm});
            skLineSegment(sketch, "E223.MirrorCS", {"start": v(16.99, 8.13) * mm, "end": v(14.99, 8.13) * mm});
            skLineSegment(sketch, "E224.MirrorCS", {"start": v(17, 9.12) * mm, "end": v(16.99, 6.63) * mm, "construction": true});
            skArc(sketch, "E225.MirrorCS", {"start": v(14.5, 9.62) * mm, "mid": v(14.65, 9.27) * mm, "end": v(15, 9.12) * mm});
            skLineSegment(sketch, "E226.MirrorCS", {"start": v(17, 9.13) * mm, "end": v(15, 9.12) * mm});
            skArc(sketch, "E227.MirrorCS", {"start": v(17.5, 10.12) * mm, "mid": v(17.35, 10.48) * mm, "end": v(17, 10.62) * mm});
            skLineSegment(sketch, "E228.MirrorCS", {"start": v(16.99, 6.63) * mm, "end": v(14.99, 6.63) * mm});
            skArc(sketch, "E229.MirrorCS", {"start": v(17, 9.12) * mm, "mid": v(17.35, 9.27) * mm, "end": v(17.5, 9.62) * mm});
            skLineSegment(sketch, "E230.MirrorCS", {"start": v(17, 10.63) * mm, "end": v(15, 10.62) * mm});
            skCircle(sketch, "E231", {"center": v(12.44, 11.36) * mm, "radius": 0.5 * mm});
            skLineSegment(sketch, "E232.2.0.0", {"start": v(-16.97, 3.13) * mm, "end": v(-14.97, 3.13) * mm});
            skLineSegment(sketch, "E232.2.0.1", {"start": v(-16.97, 1.63) * mm, "end": v(-14.97, 1.63) * mm});
            skArc(sketch, "E232.2.0.2", {"start": v(-16.97, 1.63) * mm, "mid": v(-17.32, 1.77) * mm, "end": v(-17.47, 2.13) * mm});
            skArc(sketch, "E232.2.0.3", {"start": v(-17.47, 2.63) * mm, "mid": v(-17.32, 2.98) * mm, "end": v(-16.97, 3.13) * mm});
            skArc(sketch, "E232.2.0.4", {"start": v(-14.47, 2.13) * mm, "mid": v(-14.62, 1.77) * mm, "end": v(-14.97, 1.63) * mm});
            skArc(sketch, "E232.2.0.5", {"start": v(-14.97, 3.13) * mm, "mid": v(-14.62, 2.98) * mm, "end": v(-14.47, 2.63) * mm});
            skLineSegment(sketch, "E232.2.0.6", {"start": v(-17.47, 2.63) * mm, "end": v(-17.47, 2.13) * mm});
            skLineSegment(sketch, "E232.2.0.7", {"start": v(-14.47, 2.63) * mm, "end": v(-14.47, 2.13) * mm});
            skLineSegment(sketch, "E233.1.0.0", {"start": v(-16.95, 1.13) * mm, "end": v(-14.95, 1.13) * mm});
            skLineSegment(sketch, "E233.1.0.1", {"start": v(-16.95, -0.37) * mm, "end": v(-14.95, -0.37) * mm});
            skArc(sketch, "E233.1.0.2", {"start": v(-16.95, -0.37) * mm, "mid": v(-17.3, -0.23) * mm, "end": v(-17.45, 0.13) * mm});
            skArc(sketch, "E233.1.0.3", {"start": v(-17.45, 0.63) * mm, "mid": v(-17.3, 0.98) * mm, "end": v(-16.95, 1.13) * mm});
            skArc(sketch, "E233.1.0.4", {"start": v(-14.45, 0.13) * mm, "mid": v(-14.6, -0.23) * mm, "end": v(-14.95, -0.37) * mm});
            skArc(sketch, "E233.1.0.5", {"start": v(-14.95, 1.13) * mm, "mid": v(-14.6, 0.98) * mm, "end": v(-14.45, 0.63) * mm});
            skLineSegment(sketch, "E233.1.0.6", {"start": v(-14.45, 0.63) * mm, "end": v(-14.45, 0.13) * mm});
            skLineSegment(sketch, "E233.1.0.7", {"start": v(-17.45, 0.63) * mm, "end": v(-17.45, 0.13) * mm});
            skLineSegment(sketch, "E233.2.0.0", {"start": v(-16.92, -0.87) * mm, "end": v(-14.92, -0.87) * mm});
            skLineSegment(sketch, "E233.2.0.1", {"start": v(-16.92, -2.37) * mm, "end": v(-14.92, -2.37) * mm});
            skArc(sketch, "E233.2.0.2", {"start": v(-16.92, -2.37) * mm, "mid": v(-17.28, -2.23) * mm, "end": v(-17.42, -1.87) * mm});
            skArc(sketch, "E233.2.0.3", {"start": v(-17.42, -1.37) * mm, "mid": v(-17.28, -1.02) * mm, "end": v(-16.92, -0.87) * mm});
            skArc(sketch, "E233.2.0.4", {"start": v(-14.42, -1.87) * mm, "mid": v(-14.57, -2.23) * mm, "end": v(-14.92, -2.37) * mm});
            skArc(sketch, "E233.2.0.5", {"start": v(-14.92, -0.87) * mm, "mid": v(-14.57, -1.02) * mm, "end": v(-14.42, -1.37) * mm});
            skLineSegment(sketch, "E233.2.0.6", {"start": v(-14.42, -1.37) * mm, "end": v(-14.42, -1.87) * mm});
            skLineSegment(sketch, "E233.2.0.7", {"start": v(-17.42, -1.37) * mm, "end": v(-17.42, -1.87) * mm});
            skLineSegment(sketch, "E233.3.0.0", {"start": v(-16.9, -2.87) * mm, "end": v(-14.9, -2.87) * mm});
            skLineSegment(sketch, "E233.3.0.1", {"start": v(-16.9, -4.37) * mm, "end": v(-14.9, -4.37) * mm});
            skArc(sketch, "E233.3.0.2", {"start": v(-16.9, -4.37) * mm, "mid": v(-17.25, -4.23) * mm, "end": v(-17.4, -3.87) * mm});
            skArc(sketch, "E233.3.0.3", {"start": v(-17.4, -3.37) * mm, "mid": v(-17.25, -3.02) * mm, "end": v(-16.9, -2.87) * mm});
            skArc(sketch, "E233.3.0.4", {"start": v(-14.4, -3.87) * mm, "mid": v(-14.55, -4.23) * mm, "end": v(-14.9, -4.37) * mm});
            skArc(sketch, "E233.3.0.5", {"start": v(-14.9, -2.87) * mm, "mid": v(-14.55, -3.02) * mm, "end": v(-14.4, -3.37) * mm});
            skLineSegment(sketch, "E233.3.0.6", {"start": v(-14.4, -3.37) * mm, "end": v(-14.4, -3.87) * mm});
            skLineSegment(sketch, "E233.3.0.7", {"start": v(-17.4, -3.37) * mm, "end": v(-17.4, -3.87) * mm});
            skLineSegment(sketch, "E233.direction1", {"start": v(-16.97, 1.63) * mm, "end": v(-16.95, -0.37) * mm, "construction": true});
            skLineSegment(sketch, "E234.bottom", {"start": v(-14.42, -4.87) * mm, "end": v(-17.58, -4.87) * mm});
            skLineSegment(sketch, "E234.top", {"start": v(-14.42, -6.82) * mm, "end": v(-17.58, -6.82) * mm});
            skLineSegment(sketch, "E234.left", {"start": v(-14.42, -4.87) * mm, "end": v(-14.42, -6.82) * mm});
            skLineSegment(sketch, "E234.right", {"start": v(-17.58, -4.87) * mm, "end": v(-17.58, -6.82) * mm});
            skPoint(sketch, "E234.middle", {"position": v(-16, -5.85) * mm});
            skLineSegment(sketch, "E235.1.0.0", {"start": v(-14.43, -7.57) * mm, "end": v(-17.59, -7.57) * mm});
            skLineSegment(sketch, "E235.1.0.1", {"start": v(-14.43, -9.52) * mm, "end": v(-17.59, -9.52) * mm});
            skLineSegment(sketch, "E235.1.0.2", {"start": v(-14.43, -7.57) * mm, "end": v(-14.43, -9.52) * mm});
            skLineSegment(sketch, "E235.1.0.3", {"start": v(-17.59, -7.57) * mm, "end": v(-17.59, -9.52) * mm});
            skPoint(sketch, "E235.1.0.4", {"position": v(-16, -8.55) * mm});
            skLineSegment(sketch, "E235.direction1", {"start": v(-17.58, -6.82) * mm, "end": v(-17.59, -9.52) * mm, "construction": true});
            skSolve(sketch);
        }
        {
            var Q0;
            Q0 = qSketchRegion(id + "F2", true);
            extrude(context, id + "F3", {"entities" : qUnion([Q0]), "operationType" : NewBodyOperationType.REMOVE, "oppositeDirection" : true, "depth" : .1 * mm, "offsetDistance" : 25 * mm});
        }
        {
            var Q0;
            Q0=makeQuery(id+"F1.opExtrude","CAP_FACE",FACE,{"disambiguationData":[OSD([sQuery(id+"F0.wireOp",EDGE,"E0.bottom"),sQuery(id+"F0.wireOp",EDGE,"E0.top"),sQuery(id+"F0.wireOp",EDGE,"E0.left"),sQuery(id+"F0.wireOp",EDGE,"E0.right"),sQuery(id+"F0.wireOp",EDGE,"E2"),sQuery(id+"F0.wireOp",EDGE,"E3.MirrorC"),sQuery(id+"F0.wireOp",EDGE,"E4.MirrorC"),sQuery(id+"F0.wireOp",EDGE,"E5.MirrorC"),sQuery(id+"F0.wireOp",EDGE,"E7"),sQuery(id+"F0.wireOp",EDGE,"E8.MirrorCS"),sQuery(id+"F0.wireOp",EDGE,"E9.MirrorCS"),sQuery(id+"F0.wireOp",EDGE,"E10.MirrorCS"),sQuery(id+"F0.wireOp",EDGE,"E11.trimOffspring"),sQuery(id+"F0.wireOp",EDGE,"E12.trimOffspring"),sQuery(id+"F0.wireOp",EDGE,"E13.trimOffspring"),sQuery(id+"F0.wireOp",EDGE,"E14.trimOffspring"),sQuery(id+"F0.wireOp",EDGE,"E15.filletArc"),sQuery(id+"F0.wireOp",EDGE,"E16.filletArc"),sQuery(id+"F0.wireOp",EDGE,"E17.filletArc"),sQuery(id+"F0.wireOp",EDGE,"E18.filletArc"),sQuery(id+"F0.wireOp",EDGE,"E19.filletArc"),sQuery(id+"F0.wireOp",EDGE,"E20.filletArc"),sQuery(id+"F0.wireOp",EDGE,"E21.filletArc"),sQuery(id+"F0.wireOp",EDGE,"E22.filletArc"),sQuery(id+"F0.wireOp",EDGE,"E23.filletArc"),sQuery(id+"F0.wireOp",EDGE,"E24.filletArc"),sQuery(id+"F0.wireOp",EDGE,"E25.filletArc"),sQuery(id+"F0.wireOp",EDGE,"E26.filletArc")])],"isStart":false});
            var sketch = newSketch(context, id + "F4", { "sketchPlane" : qUnion([Q0])});
            skLineSegment(sketch, "E236.bottom", {"start": v(11, -0.5) * mm, "end": v(6, -0.5) * mm});
            skLineSegment(sketch, "E236.top", {"start": v(11, 4.5) * mm, "end": v(6, 4.5) * mm});
            skLineSegment(sketch, "E236.left", {"start": v(11, -0.5) * mm, "end": v(11, 4.5) * mm});
            skLineSegment(sketch, "E236.right", {"start": v(6, -0.5) * mm, "end": v(6, 4.5) * mm});
            skPoint(sketch, "E236.middle", {"position": v(8.5, 2) * mm});
            skLineSegment(sketch, "E237.bottom", {"start": v(1, -2) * mm, "end": v(-3, -2) * mm});
            skLineSegment(sketch, "E237.top", {"start": v(1, 2) * mm, "end": v(-3, 2) * mm});
            skLineSegment(sketch, "E237.left", {"start": v(1, -2) * mm, "end": v(1, 2) * mm});
            skLineSegment(sketch, "E237.right", {"start": v(-3, -2) * mm, "end": v(-3, 2) * mm});
            skPoint(sketch, "E237.middle", {"position": v(-1, 0) * mm});
            skLineSegment(sketch, "E238.bottom", {"start": v(14, -6) * mm, "end": v(17.5, -6) * mm});
            skLineSegment(sketch, "E238.top", {"start": v(14, -10.5) * mm, "end": v(17.5, -10.5) * mm});
            skLineSegment(sketch, "E238.left", {"start": v(14, -6) * mm, "end": v(14, -10.5) * mm});
            skLineSegment(sketch, "E238.right", {"start": v(17.5, -6) * mm, "end": v(17.5, -10.5) * mm});
            skPoint(sketch, "E238.middle", {"position": v(15.75, -8.25) * mm});
            skEllipse(sketch, "E239", {"center": v(15.75, -8.25) * mm, "majorRadius": 1.2 * mm, "minorRadius": 0.7 * mm, "majorAxis": v(0, -1)});
            skLineSegment(sketch, "E240.bottom", {"start": v(-6.25, -0.28) * mm, "end": v(-9.75, -0.28) * mm});
            skLineSegment(sketch, "E240.top", {"start": v(-6.25, 1.22) * mm, "end": v(-9.75, 1.22) * mm});
            skLineSegment(sketch, "E240.left", {"start": v(-6.25, -0.28) * mm, "end": v(-6.25, 1.22) * mm});
            skLineSegment(sketch, "E240.right", {"start": v(-9.75, -0.28) * mm, "end": v(-9.75, 1.22) * mm});
            skPoint(sketch, "E240.middle", {"position": v(-8, 0.47) * mm});
            skLineSegment(sketch, "E241.1.0.0", {"start": v(-6.24, -2.48) * mm, "end": v(-6.24, -0.98) * mm});
            skLineSegment(sketch, "E241.1.0.1", {"start": v(-6.24, -0.98) * mm, "end": v(-9.74, -0.98) * mm});
            skLineSegment(sketch, "E241.1.0.2", {"start": v(-6.24, -2.48) * mm, "end": v(-9.74, -2.48) * mm});
            skPoint(sketch, "E241.1.0.3", {"position": v(-7.99, -1.73) * mm});
            skLineSegment(sketch, "E241.1.0.4", {"start": v(-9.74, -2.48) * mm, "end": v(-9.74, -0.98) * mm});
            skLineSegment(sketch, "E241.2.0.0", {"start": v(-6.22, -4.68) * mm, "end": v(-6.22, -3.18) * mm});
            skLineSegment(sketch, "E241.2.0.1", {"start": v(-6.22, -3.18) * mm, "end": v(-9.72, -3.18) * mm});
            skLineSegment(sketch, "E241.2.0.2", {"start": v(-6.22, -4.68) * mm, "end": v(-9.72, -4.68) * mm});
            skPoint(sketch, "E241.2.0.3", {"position": v(-7.97, -3.93) * mm});
            skLineSegment(sketch, "E241.2.0.4", {"start": v(-9.72, -4.68) * mm, "end": v(-9.72, -3.18) * mm});
            skLineSegment(sketch, "E241.direction1", {"start": v(-9.75, -0.28) * mm, "end": v(-9.74, -2.48) * mm, "construction": true});
            skLineSegment(sketch, "E242.bottom", {"start": v(18, 3.75) * mm, "end": v(12, 3.75) * mm});
            skLineSegment(sketch, "E242.top", {"start": v(18, -3.75) * mm, "end": v(12, -3.75) * mm});
            skLineSegment(sketch, "E242.left", {"start": v(18, 3.75) * mm, "end": v(18, -3.75) * mm});
            skLineSegment(sketch, "E242.right", {"start": v(12, 3.75) * mm, "end": v(12, -3.75) * mm});
            skSolve(sketch);
        }
        {
            var Q0;
            Q0=makeQuery(id+"F4.imprint","IMPRINT",FACE,{"disambiguationData":[TD([[makeQuery(id+"F4.imprint","IMPRINT",EDGE,{"derivedFrom":sQuery(id+"F4.wireOp",EDGE,"E236.bottom")}),-1.0]])]});
            var Q1;
            Q1=makeQuery(id+"F4.imprint","IMPRINT",FACE,{"disambiguationData":[TD([[makeQuery(id+"F4.imprint","IMPRINT",EDGE,{"derivedFrom":sQuery(id+"F4.wireOp",EDGE,"E237.bottom")}),-1.0]])]});
            extrude(context, id + "F5", {"entities" : qUnion([Q0, Q1]), "operationType" : NewBodyOperationType.ADD, "depth" : 1 * mm, "offsetDistance" : 25 * mm});
        }
        {
            var Q0;
            Q0=makeQuery(id+"F4.imprint","IMPRINT",FACE,{"disambiguationData":[TD([[makeQuery(id+"F4.imprint","IMPRINT",EDGE,{"derivedFrom":sQuery(id+"F4.wireOp",EDGE,"E240.bottom")}),-1.0]])]});
            var Q1;
            Q1=makeQuery(id+"F4.imprint","IMPRINT",FACE,{"disambiguationData":[TD([[makeQuery(id+"F4.imprint","IMPRINT",EDGE,{"derivedFrom":sQuery(id+"F4.wireOp",EDGE,"E241.1.0.0")}),1.0]])]});
            var Q2;
            Q2=makeQuery(id+"F4.imprint","IMPRINT",FACE,{"disambiguationData":[TD([[makeQuery(id+"F4.imprint","IMPRINT",EDGE,{"derivedFrom":sQuery(id+"F4.wireOp",EDGE,"E241.2.0.0")}),1.0]])]});
            extrude(context, id + "F6", {"entities" : qUnion([Q0, Q1, Q2]), "operationType" : NewBodyOperationType.ADD, "depth" : 2 * mm, "offsetDistance" : 25 * mm});
        }
        {
            var Q0;
            Q0=makeQuery(id+"F4.imprint","IMPRINT",FACE,{"disambiguationData":[TD([[makeQuery(id+"F4.imprint","IMPRINT",EDGE,{"derivedFrom":sQuery(id+"F4.wireOp",EDGE,"E242.bottom")}),1.0]])]});
            var Q1;
            Q1=makeQuery(id+"F4.imprint","IMPRINT",FACE,{"disambiguationData":[TD([[makeQuery(id+"F4.imprint","IMPRINT",EDGE,{"derivedFrom":sQuery(id+"F4.wireOp",EDGE,"E239")}),1.0]])]});
            extrude(context, id + "F7", {"entities" : qUnion([Q0, Q1]), "operationType" : NewBodyOperationType.ADD, "depth" : 3 * mm, "offsetDistance" : 25 * mm});
        }
        {
            var Q0;
            Q0=makeQuery(id+"F4.imprint","IMPRINT",FACE,{"disambiguationData":[TD([[makeQuery(id+"F4.imprint","IMPRINT",EDGE,{"derivedFrom":sQuery(id+"F4.wireOp",EDGE,"E238.bottom")}),-1.0]])]});
            extrude(context, id + "F8", {"entities" : qUnion([Q0]), "operationType" : NewBodyOperationType.ADD, "depth" : 2 * mm, "offsetDistance" : 25 * mm});
        }
    });
